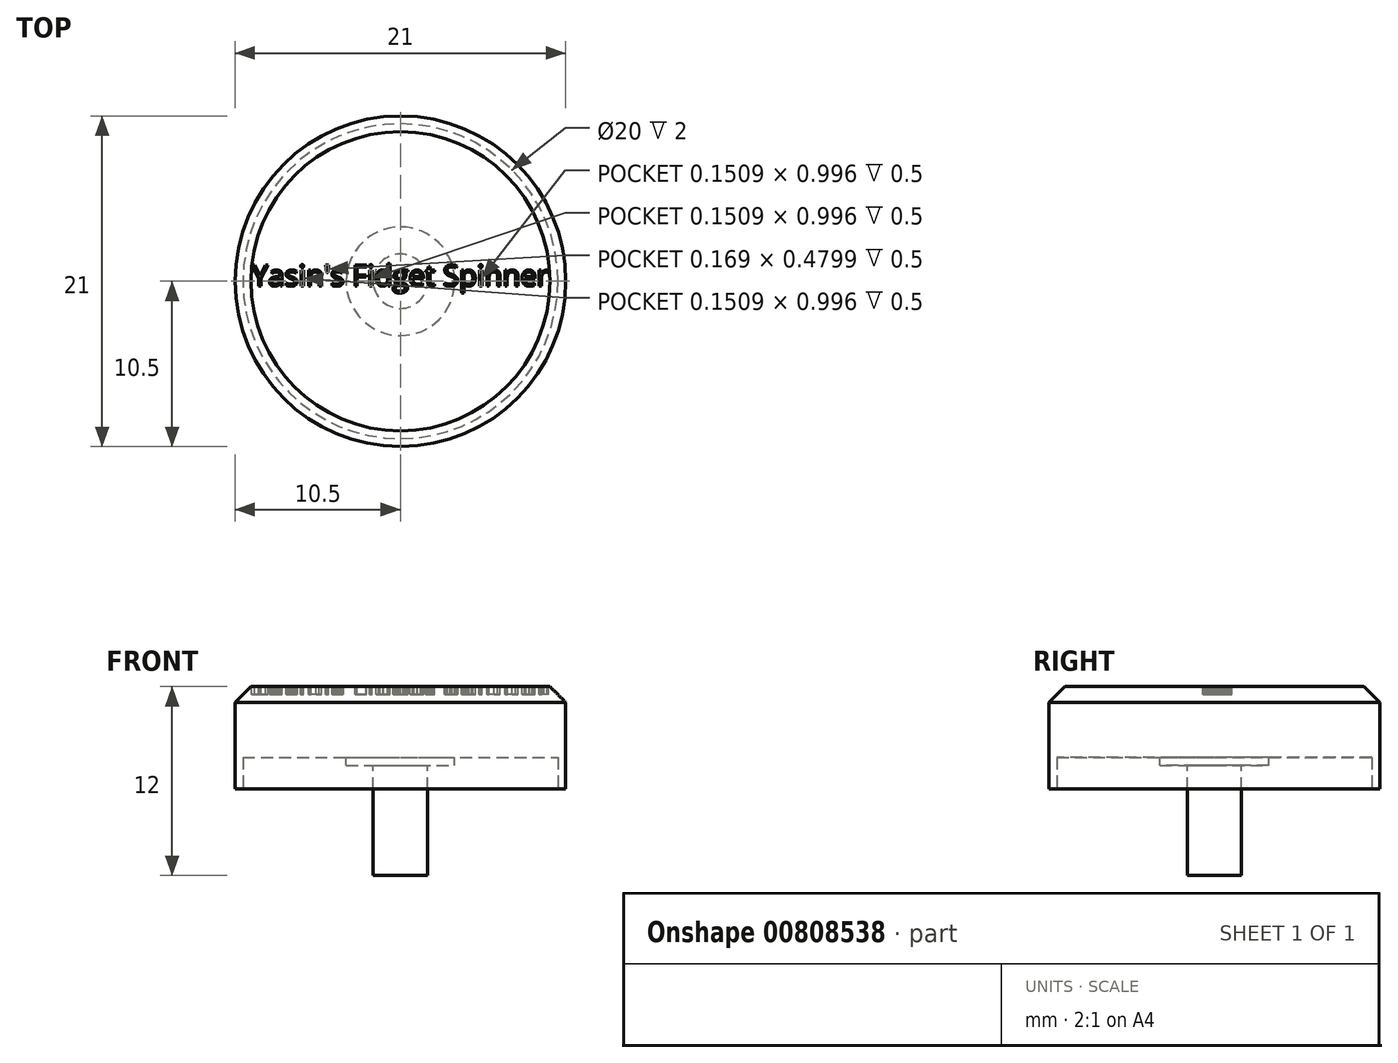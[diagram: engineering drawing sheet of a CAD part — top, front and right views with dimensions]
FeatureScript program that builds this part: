
annotation { "Feature Type Name" : "Feature", "Feature Type Description" : "" }
export const myFeature = defineFeature(function(context is Context, id is Id, definition is map)
    precondition{}
    {
        {
            var Q0;
            Q0=qCreatedBy(makeId("Top.planeOp"),FACE);
            var sketch = newSketch(context, id + "F0", { "sketchPlane" : qUnion([Q0])});
            skCircle(sketch, "E0", {"center": v(0, 0) * mm, "radius": 10.5 * mm});
            skSolve(sketch);
        }
        {
            var Q0;
            Q0=makeQuery(id+"F0.imprint","IMPRINT",FACE,{"disambiguationData":[TD([[makeQuery(id+"F0.imprint","IMPRINT",EDGE,{"derivedFrom":sQuery(id+"F0.wireOp",EDGE,"E0")}),1.0]])]});
            extrude(context, id + "F1", {"entities" : qUnion([Q0]), "depth" : 4 * mm, "offsetDistance" : 25 * mm});
        }
        {
            var Q0;
            Q0=makeQuery(id+"F1.opExtrude","CAP_FACE",FACE,{"disambiguationData":[OSD([sQuery(id+"F0.wireOp",EDGE,"E0")])],"isStart":true});
            var sketch = newSketch(context, id + "F2", { "sketchPlane" : qUnion([Q0])});
            skCircle(sketch, "E1", {"center": v(0, 0) * mm, "radius": 10 * mm});
            skSolve(sketch);
        }
        {
            var Q0;
            Q0=makeQuery(id+"F2.imprint","IMPRINT",FACE,{"disambiguationData":[TD([[makeQuery(id+"F2.imprint","IMPRINT",EDGE,{"derivedFrom":sQuery(id+"F2.wireOp",EDGE,"E1")}),1.0]])]});
            extrude(context, id + "F3", {"entities" : qUnion([Q0]), "operationType" : NewBodyOperationType.REMOVE, "oppositeDirection" : true, "depth" : 2 * mm, "offsetDistance" : 25 * mm});
        }
        {
            var Q0;
            Q0=makeQuery(id+"F3.boolean.opBoolean","COPY",FACE,{"derivedFrom":makeQuery(id+"F3.opExtrude","CAP_FACE",FACE,{"disambiguationData":[OSD([sQuery(id+"F2.wireOp",EDGE,"E1")])],"isStart":false})});
            var sketch = newSketch(context, id + "F4", { "sketchPlane" : qUnion([Q0])});
            skCircle(sketch, "E2", {"center": v(0, 0) * mm, "radius": 3.45 * mm});
            skCircle(sketch, "E3", {"center": v(0, 0) * mm, "radius": 1.73 * mm});
            skSolve(sketch);
        }
        {
            var Q0;
            Q0=makeQuery(id+"F4.imprint","IMPRINT",FACE,{"disambiguationData":[TD([[makeQuery(id+"F4.imprint","IMPRINT",EDGE,{"derivedFrom":sQuery(id+"F4.wireOp",EDGE,"E2")}),1.0]])]});
            extrude(context, id + "F5", {"entities" : qUnion([Q0]), "operationType" : NewBodyOperationType.ADD, "depth" : 0.5 * mm, "offsetDistance" : 25 * mm});
        }
        {
            var Q0;
            Q0=makeQuery(id+"F5.boolean.opBoolean","SPLIT",FACE,{"disambiguationData":[TD([makeQuery(id+"F5.opExtrude","SWEPT_FACE",FACE,{"disambiguationData":[OSD([sQuery(id+"F4.wireOp",EDGE,"E3")])]})])],"derivedFrom":makeQuery(id+"F3.boolean.opBoolean","COPY",FACE,{"derivedFrom":makeQuery(id+"F3.opExtrude","CAP_FACE",FACE,{"disambiguationData":[OSD([sQuery(id+"F2.wireOp",EDGE,"E1")])],"isStart":false})})});
            extrude(context, id + "F6", {"entities" : qUnion([Q0]), "operationType" : NewBodyOperationType.ADD, "depth" : 7.5 * mm, "offsetDistance" : 25 * mm});
        }
        {
            var Q0;
            Q0=makeQuery(id+"F1.opExtrude","CAP_FACE",FACE,{"disambiguationData":[OSD([sQuery(id+"F0.wireOp",EDGE,"E0")])],"isStart":false});
            extrude(context, id + "F7", {"entities" : qUnion([Q0]), "operationType" : NewBodyOperationType.ADD, "depth" : 2.5 * mm, "offsetDistance" : 25 * mm});
        }
        {
            var Q0;
            Q0=makeQuery(id+"F7.opExtrude","CAP_EDGE",EDGE,{"disambiguationData":[OSD([sQuery(id+"F0.wireOp",EDGE,"E0")])],"isStart":false});
            chamfer(context, id + "F8", {"entities" : qUnion([Q0]), "width" : 1 * mm, "tangentPropagation" : true});
        }
        {
            var Q0;
            Q0=makeQuery(id+"F7.opExtrude","CAP_FACE",FACE,{"disambiguationData":[OSD([sQuery(id+"F0.wireOp",EDGE,"E0")])],"isStart":false});
            var sketch = newSketch(context, id + "F9", { "sketchPlane" : qUnion([Q0])});
            skText(sketch, "E4", { "text": "Yasin\'s Fidget Spinner", "fontName": "OpenSans-Regular.ttf"});
            const initialGuessF9  = {"E4": [-0.00944, -0.0003, 1, 0, 0.00134]};
            skSetInitialGuess(sketch, initialGuessF9);
            skSolve(sketch);
        }
        {
            var Q0;
            Q0 = qSketchRegion(id + "F9", true);
            extrude(context, id + "F10", {"entities" : qUnion([Q0]), "operationType" : NewBodyOperationType.REMOVE, "oppositeDirection" : true, "depth" : 0.5 * mm, "offsetDistance" : 25 * mm});
        }
    });
